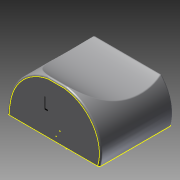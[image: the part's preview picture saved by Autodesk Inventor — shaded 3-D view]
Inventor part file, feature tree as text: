
AUTODESK INVENTOR PART (.ipt)
format: ipt  version: 2012 SP1 (Build 160190100, 190)  size: 212,992 bytes
history: native  units: in
note: dims shown in document units (in); Inventor stores cm internally (conversion verified against a paired STEP export)
features: sketch x4, extrude x2, fillet x2
ambient origin geometry x8: Origin, YZ Plane, XZ Plane, XY Plane, X Axis, Y Axis, Z Axis, Center Point
bodies: Solid1 (feature_tree)
feature tree (8):
  extrude  "Extrusion1"  Depth=0.75in TaperAngle=0.0deg
  fillet  "Fillet1"  Radius=0.0175in
  extrude  "Extrusion3"  Depth=0.015in
  fillet  "Fillet2"  [1 undecoded]
  sketch  "Sketch4"
  sketch  "Sketch5"
  sketch  "Sketch1"  dims[d0=0.85in d3=0.75in d4=0.0in d7=0.0175in]
  sketch  "Sketch3"  dims[d14=1.0in d15=0.0in d16=0.015in]
note: 1 required parameter value undecoded (feature->parameter linkage not recoverable at this tier; creation-order binding heuristic only, values carry confidence <= 0.55)
